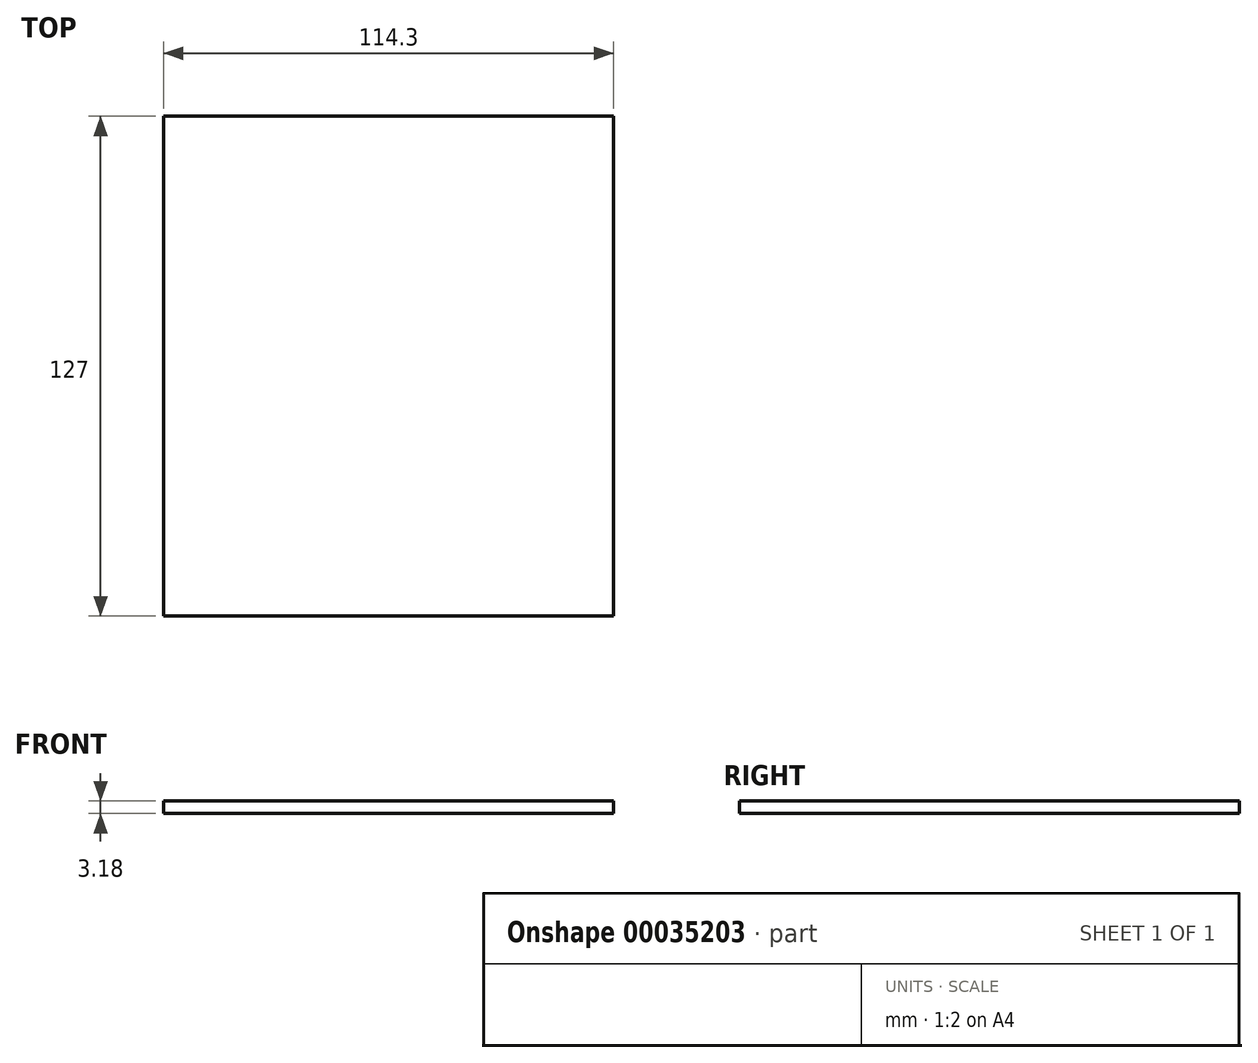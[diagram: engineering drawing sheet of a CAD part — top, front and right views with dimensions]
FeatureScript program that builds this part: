
annotation { "Feature Type Name" : "Feature", "Feature Type Description" : "" }
export const myFeature = defineFeature(function(context is Context, id is Id, definition is map)
    precondition{}
    {
        {
            var Q0;
            Q0=qCreatedBy(makeId("Top.planeOp"),FACE);
            var sketch = newSketch(context, id + "F0", { "sketchPlane" : qUnion([Q0])});
            skLineSegment(sketch, "E0.bottom", {"start": v(-57.89, 86.15) * mm, "end": v(56.41, 86.15) * mm});
            skLineSegment(sketch, "E0.top", {"start": v(-57.89, -40.85) * mm, "end": v(56.41, -40.85) * mm});
            skLineSegment(sketch, "E0.left", {"start": v(-57.89, 86.15) * mm, "end": v(-57.89, -40.85) * mm});
            skLineSegment(sketch, "E0.right", {"start": v(56.41, 86.15) * mm, "end": v(56.41, -40.85) * mm});
            skSolve(sketch);
        }
        {
            var Q0;
            Q0=makeQuery(id+"F0.imprint","IMPRINT",FACE,{"disambiguationData":[TD([[makeQuery(id+"F0.imprint","IMPRINT",EDGE,{"derivedFrom":sQuery(id+"F0.wireOp",EDGE,"E0.bottom")}),-1.0]])]});
            extrude(context, id + "F1", {"entities" : qUnion([Q0]), "depth" : 3.18 * mm});
        }
    });
